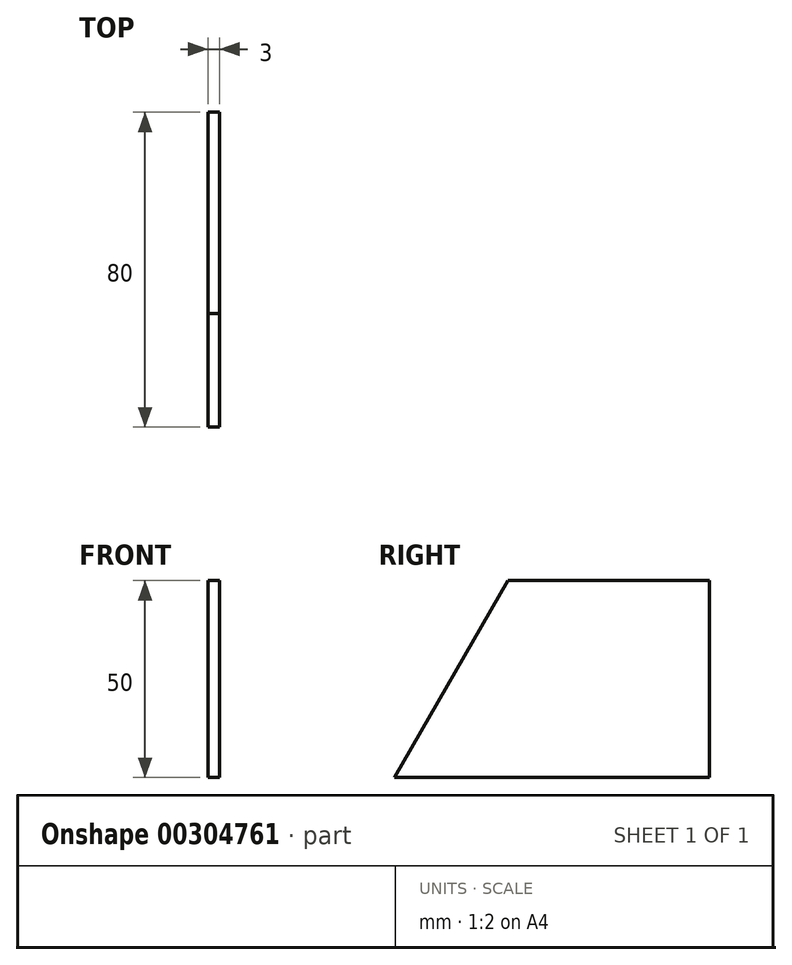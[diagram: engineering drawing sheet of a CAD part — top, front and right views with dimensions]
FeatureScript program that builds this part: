
annotation { "Feature Type Name" : "Feature", "Feature Type Description" : "" }
export const myFeature = defineFeature(function(context is Context, id is Id, definition is map)
    precondition{}
    {
        {
            var Q0;
            Q0=qCreatedBy(makeId("Right.planeOp"),FACE);
            var sketch = newSketch(context, id + "F0", { "sketchPlane" : qUnion([Q0])});
            skLineSegment(sketch, "E0.bottom", {"start": v(0, 0) * mm, "end": v(80, 0) * mm});
            skLineSegment(sketch, "E0.top", {"start": v(28.87, 50) * mm, "end": v(80, 50) * mm});
            skLineSegment(sketch, "E0.right", {"start": v(80, 0) * mm, "end": v(80, 50) * mm});
            skLineSegment(sketch, "E1", {"start": v(0, 0) * mm, "end": v(28.87, 50) * mm});
            skSolve(sketch);
        }
        {
            var Q0;
            Q0 = qSketchRegion(id + "F0", true);
            extrude(context, id + "F1", {"entities" : qUnion([Q0]), "depth" : 3 * mm});
        }
    });
